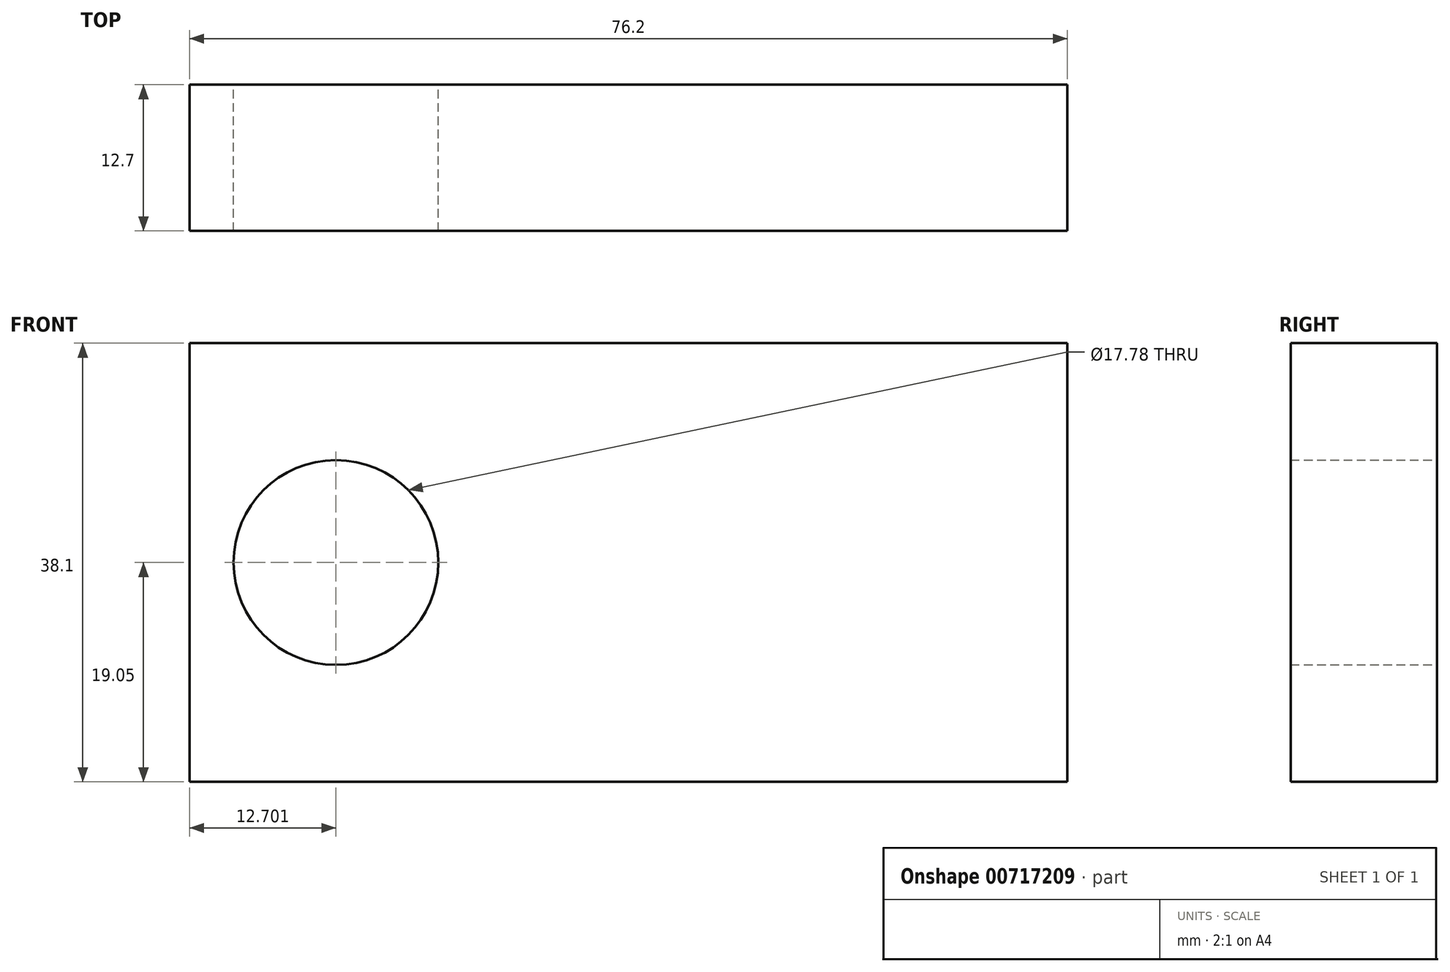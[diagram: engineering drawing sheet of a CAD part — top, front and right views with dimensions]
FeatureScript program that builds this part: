
annotation { "Feature Type Name" : "Feature", "Feature Type Description" : "" }
export const myFeature = defineFeature(function(context is Context, id is Id, definition is map)
    precondition{}
    {
        {
            var Q0;
            Q0=qCreatedBy(makeId("Front.planeOp"),FACE);
            var sketch = newSketch(context, id + "F0", { "sketchPlane" : qUnion([Q0])});
            skLineSegment(sketch, "E0.bottom", {"start": v(-33.9, 19.05) * mm, "end": v(42.3, 19.05) * mm});
            skLineSegment(sketch, "E0.top", {"start": v(-33.9, -19.05) * mm, "end": v(42.3, -19.05) * mm});
            skLineSegment(sketch, "E0.left", {"start": v(-33.9, 19.05) * mm, "end": v(-33.9, -19.05) * mm});
            skLineSegment(sketch, "E0.right", {"start": v(42.3, 19.05) * mm, "end": v(42.3, -19.05) * mm});
            skCircle(sketch, "E1", {"center": v(-21.2, 0) * mm, "radius": 8.9 * mm});
            skSolve(sketch);
        }
        {
            var Q0;
            Q0 = qSketchRegion(id + "F0", true);
            extrude(context, id + "F1", {"entities" : qUnion([Q0]), "depth" : 12.7 * mm, "offsetDistance" : 25.4 * mm});
        }
    });
